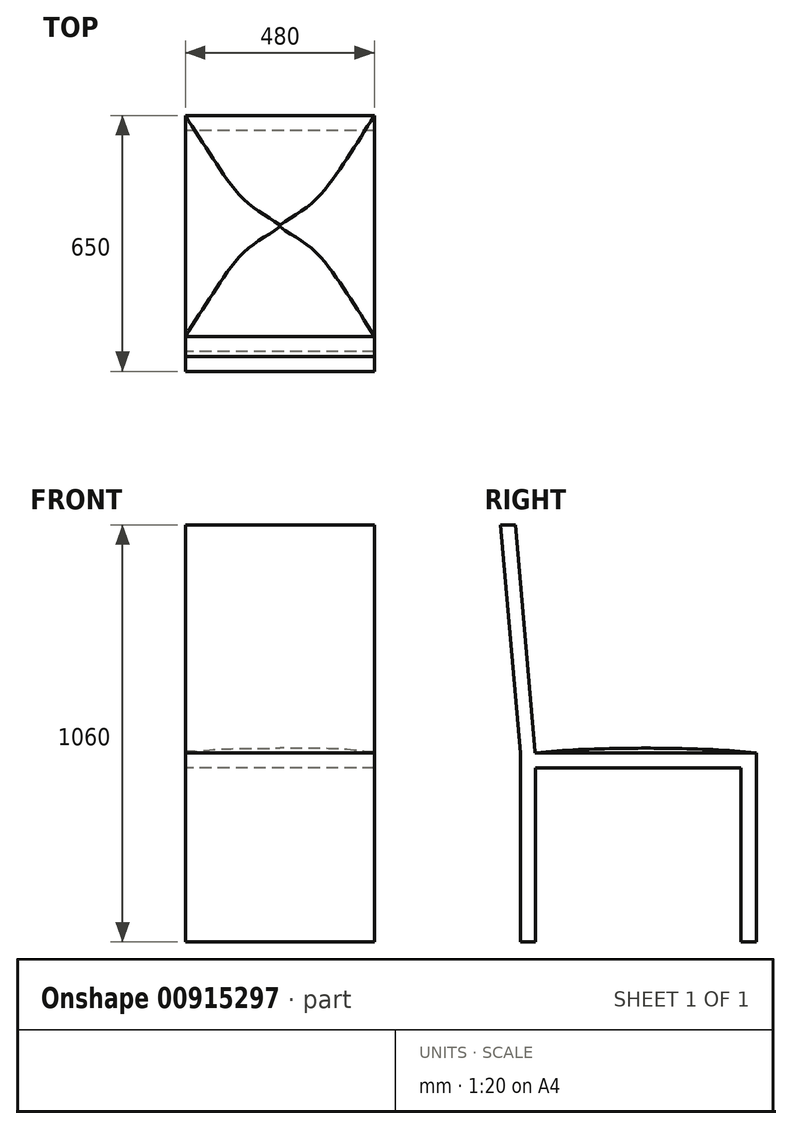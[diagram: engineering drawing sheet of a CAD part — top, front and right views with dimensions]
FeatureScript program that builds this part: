
annotation { "Feature Type Name" : "Feature", "Feature Type Description" : "" }
export const myFeature = defineFeature(function(context is Context, id is Id, definition is map)
    precondition{}
    {
        {
            var Q0;
            Q0=qCreatedBy(makeId("Right.planeOp"),FACE);
            var sketch = newSketch(context, id + "F0", { "sketchPlane" : qUnion([Q0])});
            skLineSegment(sketch, "E0", {"start": v(-50.48, -545.68) * mm, "end": v(-50.48, 514.32) * mm, "construction": true});
            skLineSegment(sketch, "E1", {"start": v(-50.48, -545.68) * mm, "end": v(599.52, -545.68) * mm, "construction": true});
            skLineSegment(sketch, "E2", {"start": v(599.52, -545.68) * mm, "end": v(599.52, -65.68) * mm, "construction": true});
            skLineSegment(sketch, "E3", {"start": v(599.52, -65.68) * mm, "end": v(599.52, -545.68) * mm});
            skLineSegment(sketch, "E4", {"start": v(599.52, -545.68) * mm, "end": v(561.42, -545.68) * mm});
            skLineSegment(sketch, "E5", {"start": v(561.42, -545.68) * mm, "end": v(561.42, -103.78) * mm});
            skLineSegment(sketch, "E6", {"start": v(561.42, -65.68) * mm, "end": v(561.42, -103.78) * mm, "construction": true});
            skLineSegment(sketch, "E7", {"start": v(561.42, -65.68) * mm, "end": v(599.52, -65.68) * mm});
            skLineSegment(sketch, "E8", {"start": v(-50.48, -498.23) * mm, "end": v(0.32, -498.23) * mm, "construction": true});
            skLineSegment(sketch, "E9", {"start": v(0.32, -545.68) * mm, "end": v(0.32, -65.68) * mm});
            skLineSegment(sketch, "E10", {"start": v(0.32, -545.68) * mm, "end": v(38.42, -545.68) * mm});
            skLineSegment(sketch, "E11", {"start": v(38.42, -103.78) * mm, "end": v(38.42, -545.68) * mm});
            skLineSegment(sketch, "E12", {"start": v(38.42, -103.78) * mm, "end": v(38.42, -65.68) * mm, "construction": true});
            skLineSegment(sketch, "E13", {"start": v(38.42, -65.68) * mm, "end": v(0.32, -65.68) * mm});
            skLineSegment(sketch, "E14", {"start": v(38.42, -65.68) * mm, "end": v(561.42, -65.68) * mm});
            skLineSegment(sketch, "E15", {"start": v(38.42, -103.78) * mm, "end": v(561.42, -103.78) * mm});
            skLineSegment(sketch, "E16", {"start": v(-50.48, 514.32) * mm, "end": v(-12.38, 514.32) * mm});
            skLineSegment(sketch, "E17", {"start": v(0.32, -65.68) * mm, "end": v(-50.48, 514.32) * mm});
            skLineSegment(sketch, "E18", {"start": v(-12.38, 514.32) * mm, "end": v(38.42, -65.68) * mm});
            skSolve(sketch);
        }
        {
            var Q0;
            Q0 = qSketchRegion(id + "F0", true);
            extrude(context, id + "F1", {"entities" : qUnion([Q0]), "depth" : 240 * mm, "offsetDistance" : 25.4 * mm});
        }
        {
            var Q0;
            Q0=qCreatedBy(makeId("Right.planeOp"),FACE);
            var sketch = newSketch(context, id + "F2", { "sketchPlane" : qUnion([Q0])});
            skLineSegment(sketch, "E19", {"start": v(38.42, -65.68) * mm, "end": v(318.97, -65.68) * mm});
            skLineSegment(sketch, "E20", {"start": v(318.97, -65.68) * mm, "end": v(318.97, -52.98) * mm});
            skFitSpline(sketch, "E21", {"points": [v(318.97, -52.98) * mm, v(146.44, -56.91) * mm, v(38.42, -65.68) * mm], "startDerivative": vector(-294.88, -3.98) * mm, "endDerivative": vector(-226.13, -21.94) * mm});
            skFitSpline(sketch, "E22.MirrorCS", {"points": [v(318.97, -52.98) * mm, v(491.5, -56.91) * mm, v(599.52, -65.68) * mm], "startDerivative": vector(294.88, -3.98) * mm, "endDerivative": vector(226.13, -21.94) * mm});
            skLineSegment(sketch, "E23.MirrorCS", {"start": v(599.52, -65.68) * mm, "end": v(318.97, -65.68) * mm});
            skSolve(sketch);
        }
        {
            var Q0;
            Q0=qCreatedBy(makeId("Front.planeOp"),FACE);
            cPlane(context, id + "F3", {"entities" : qUnion([Q0]), "cplaneType" : CPlaneType.OFFSET, "offset" : 38.1 * mm, "oppositeDirection" : true, "width" : 152.4 * mm, "height" : 152.4 * mm});
        }
        {
            var Q0;
            Q0 = qSketchRegion(id + "F2", true);
            extrude(context, id + "F4", {"entities" : qUnion([Q0]), "operationType" : NewBodyOperationType.ADD, "depth" : 240 * mm, "offsetDistance" : 25.4 * mm});
        }
        {
            var Q0;
            Q0=qCreatedBy(id+"F3.planeOp",FACE);
            var sketch = newSketch(context, id + "F5", { "sketchPlane" : qUnion([Q0])});
            skFitSpline(sketch, "E24.MirrorCS", {"points": [v(0, -53) * mm, v(157.07, -55.97) * mm, v(240, -65.7) * mm], "startDerivative": vector(314.52, -3.2) * mm, "endDerivative": vector(210.02, -34.32) * mm});
            skLineSegment(sketch, "E25", {"start": v(240, -65.7) * mm, "end": v(399.3, -65.7) * mm});
            skLineSegment(sketch, "E26", {"start": v(399.3, -65.7) * mm, "end": v(399.3, 153.25) * mm});
            skLineSegment(sketch, "E27", {"start": v(399.3, 153.25) * mm, "end": v(-33.68, 153.25) * mm});
            skLineSegment(sketch, "E28", {"start": v(-33.68, 153.25) * mm, "end": v(0, -53) * mm});
            skSolve(sketch);
        }
        {
            var Q0;
            Q0 = qSketchRegion(id + "F5", true);
            extrude(context, id + "F6", {"entities" : qUnion([Q0]), "operationType" : NewBodyOperationType.REMOVE, "oppositeDirection" : true, "depth" : 762 * mm, "offsetDistance" : 25.4 * mm});
        }
        {
            var Q0;
            Q0=makeQuery(id+"F1.opExtrude","SWEPT_BODY",BODY,{"disambiguationData":[OSD([sQuery(id+"F0.wireOp",EDGE,"E3"),sQuery(id+"F0.wireOp",EDGE,"E4"),sQuery(id+"F0.wireOp",EDGE,"E5"),sQuery(id+"F0.wireOp",EDGE,"E7"),sQuery(id+"F0.wireOp",EDGE,"E9"),sQuery(id+"F0.wireOp",EDGE,"E10"),sQuery(id+"F0.wireOp",EDGE,"E11"),sQuery(id+"F0.wireOp",EDGE,"E14"),sQuery(id+"F0.wireOp",EDGE,"E15"),sQuery(id+"F0.wireOp",EDGE,"E16"),sQuery(id+"F0.wireOp",EDGE,"E17"),sQuery(id+"F0.wireOp",EDGE,"E18")])]});
            var Q1;
            Q1=qCreatedBy(makeId("Right.planeOp"),FACE);
            mirror(context, id + "F7", {"operationType" : NewBodyOperationType.ADD, "entities" : qUnion([Q0]), "mirrorPlane" : qUnion([Q1])});
        }
    });
